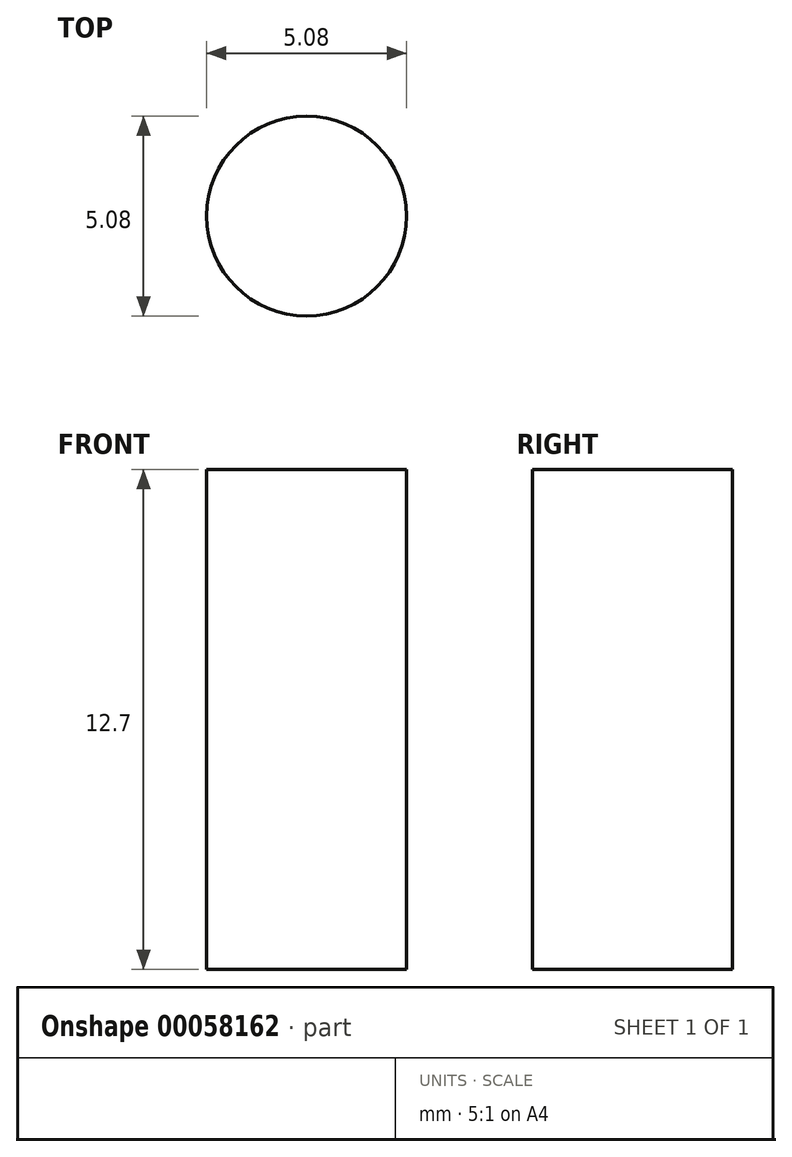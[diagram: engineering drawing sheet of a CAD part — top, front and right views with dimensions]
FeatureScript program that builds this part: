
annotation { "Feature Type Name" : "Feature", "Feature Type Description" : "" }
export const myFeature = defineFeature(function(context is Context, id is Id, definition is map)
    precondition{}
    {
        {
            var Q0;
            Q0=qCreatedBy(makeId("Top.planeOp"),FACE);
            var sketch = newSketch(context, id + "F0", { "sketchPlane" : qUnion([Q0])});
            skCircle(sketch, "E0", {"center": v(0, 0) * mm, "radius": 2.54 * mm});
            skSolve(sketch);
        }
        {
            var Q0;
            Q0=makeQuery(id+"F0.imprint","IMPRINT",FACE,{"disambiguationData":[TD([[makeQuery(id+"F0.imprint","IMPRINT",EDGE,{"derivedFrom":sQuery(id+"F0.wireOp",EDGE,"E0")}),1.0]])]});
            extrude(context, id + "F1", {"entities" : qUnion([Q0]), "depth" : 12.7 * mm, "offsetDistance" : 25.4 * mm});
        }
    });
